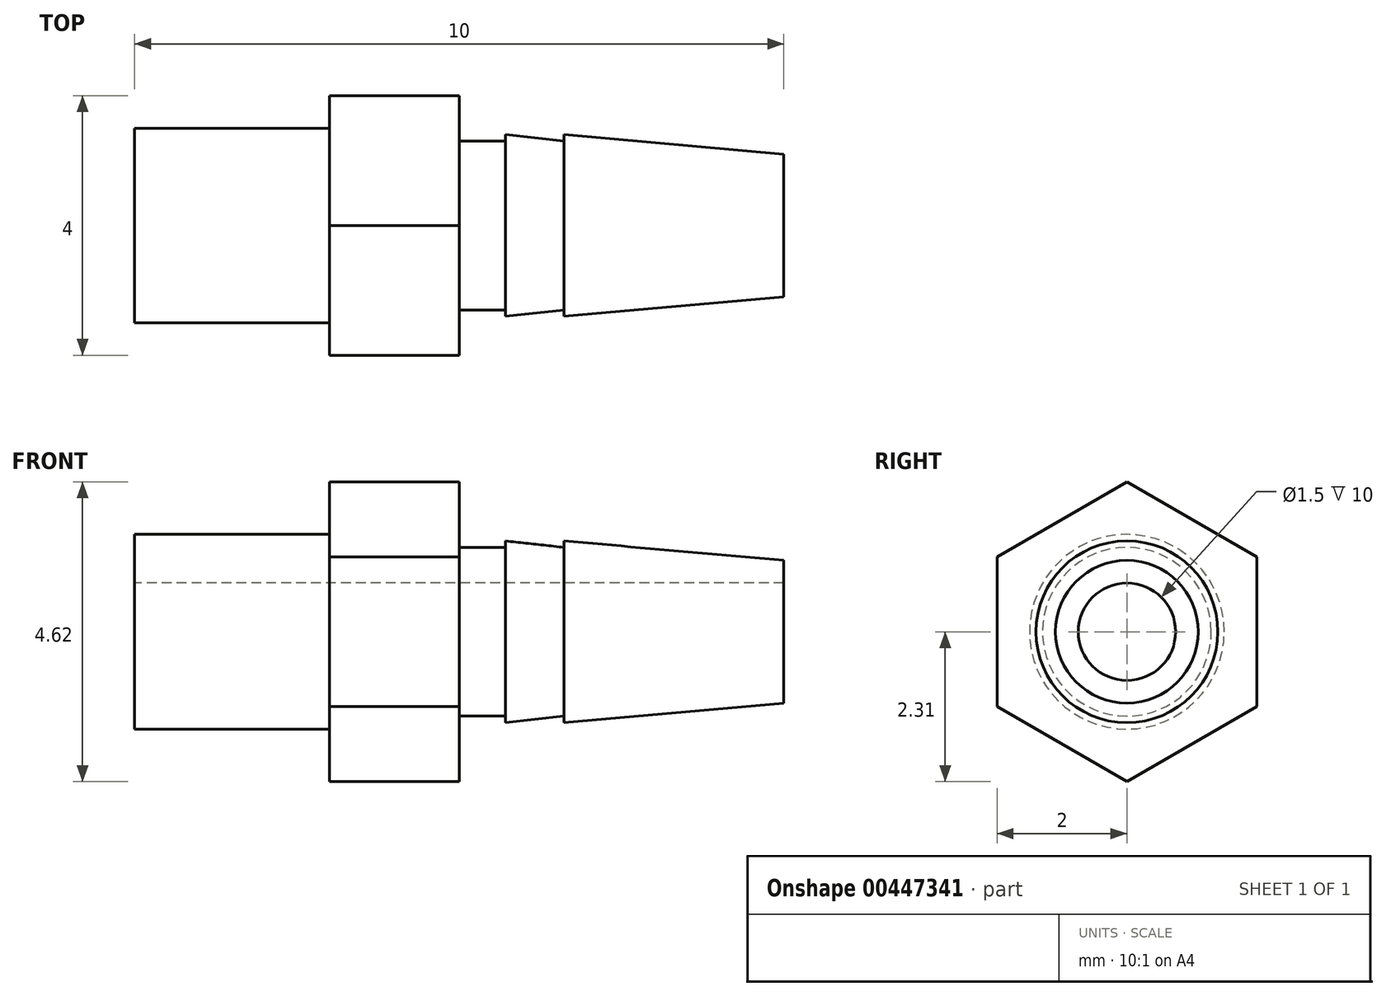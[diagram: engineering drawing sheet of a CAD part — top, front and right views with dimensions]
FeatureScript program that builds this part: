
annotation { "Feature Type Name" : "Feature", "Feature Type Description" : "" }
export const myFeature = defineFeature(function(context is Context, id is Id, definition is map)
    precondition{}
    {
        {
            var Q0;
            Q0=qCreatedBy(makeId("Top.planeOp"),FACE);
            var sketch = newSketch(context, id + "F0", { "sketchPlane" : qUnion([Q0])});
            skLineSegment(sketch, "E0", {"start": v(0, 0) * mm, "end": v(15.5, 0) * mm, "construction": true});
            skLineSegment(sketch, "E1", {"start": v(0, 0.75) * mm, "end": v(10, 0.75) * mm});
            skLineSegment(sketch, "E2", {"start": v(10, 0.75) * mm, "end": v(10, 1.1) * mm});
            skLineSegment(sketch, "E3", {"start": v(10, 1.1) * mm, "end": v(6.62, 1.4) * mm});
            skLineSegment(sketch, "E4", {"start": v(6.62, 1.4) * mm, "end": v(6.62, 1.3) * mm});
            skLineSegment(sketch, "E5", {"start": v(6.62, 1.3) * mm, "end": v(5.71, 1.4) * mm});
            skLineSegment(sketch, "E6", {"start": v(5.71, 1.4) * mm, "end": v(5.71, 1.3) * mm});
            skLineSegment(sketch, "E7", {"start": v(5.71, 1.3) * mm, "end": v(5, 1.3) * mm});
            skLineSegment(sketch, "E8", {"start": v(5, 1.3) * mm, "end": v(5, 2) * mm});
            skLineSegment(sketch, "E9", {"start": v(5, 2) * mm, "end": v(3, 2) * mm});
            skLineSegment(sketch, "E10", {"start": v(3, 2) * mm, "end": v(3, 1.5) * mm});
            skLineSegment(sketch, "E11", {"start": v(3, 1.5) * mm, "end": v(0, 1.5) * mm});
            skLineSegment(sketch, "E12", {"start": v(0, 1.5) * mm, "end": v(0, 0.75) * mm});
            skSolve(sketch);
        }
        {
            var Q0;
            Q0=makeQuery(id+"F0.imprint","IMPRINT",FACE,{"disambiguationData":[TD([[makeQuery(id+"F0.imprint","IMPRINT",EDGE,{"derivedFrom":sQuery(id+"F0.wireOp",EDGE,"E1")}),1.0]])]});
            var Q1;
            Q1=sQuery(id+"F0.wireOp",EDGE,"E0");
            revolve(context, id + "F1", {"entities" : qUnion([Q0]), "axis" : qUnion([Q1]), "revolveType" : RevolveType.FULL});
        }
        {
            var Q0;
            Q0=makeQuery(id+"F1.opRevolve","SWEPT_FACE",FACE,{"disambiguationData":[OSD([sQuery(id+"F0.wireOp",EDGE,"E8")])]});
            var sketch = newSketch(context, id + "F2", { "sketchPlane" : qUnion([Q0])});
            skLineSegment(sketch, "E13", {"start": v(0, 0) * mm, "end": v(2, 0) * mm, "construction": true});
            skCircle(sketch, "E14.cCircle", {"center": v(0, 0) * mm, "radius": 2 * mm, "construction": true});
            skLineSegment(sketch, "E14.0", {"start": v(2, 1.15) * mm, "end": v(2, -1.15) * mm});
            skLineSegment(sketch, "E14.1", {"start": v(2, -1.15) * mm, "end": v(0, -2.3) * mm});
            skLineSegment(sketch, "E14.2", {"start": v(0, -2.3) * mm, "end": v(-2, -1.15) * mm});
            skLineSegment(sketch, "E14.3", {"start": v(-2, -1.15) * mm, "end": v(-2, 1.15) * mm});
            skLineSegment(sketch, "E14.4", {"start": v(-2, 1.15) * mm, "end": v(0, 2.3) * mm});
            skLineSegment(sketch, "E14.5", {"start": v(0, 2.3) * mm, "end": v(2, 1.15) * mm});
            skPoint(sketch, "E14.0.midPoint", {"position": v(2, 0) * mm});
            skSolve(sketch);
        }
        {
            var Q0;
            {var subQ0=sQuery(id+"F2.wireOp",EDGE,"E14.3");var subQ1=sQuery(id+"F2.wireOp",EDGE,"E14.2");var subQ2=makeQuery(id+"F2.imprint","INTERSECT",VERTEX,{"derivedFrom":[subQ1,subQ0]});Q0=makeQuery(id+"F2.imprint","IMPRINT",FACE,{"disambiguationData":[TD([[makeQuery(id+"F2.imprint","IMPRINT",EDGE,{"disambiguationData":[TD([[subQ2,1.0]])],"derivedFrom":subQ1}),-1.0]])]});}
            var Q1;
            {var subQ0=sQuery(id+"F2.wireOp",EDGE,"E14.2");var subQ1=sQuery(id+"F2.wireOp",EDGE,"E14.1");var subQ2=makeQuery(id+"F2.imprint","INTERSECT",VERTEX,{"derivedFrom":[subQ1,subQ0]});Q1=makeQuery(id+"F2.imprint","IMPRINT",FACE,{"disambiguationData":[TD([[makeQuery(id+"F2.imprint","IMPRINT",EDGE,{"disambiguationData":[TD([[subQ2,1.0]])],"derivedFrom":subQ1}),-1.0]])]});}
            var Q2;
            {var subQ0=sQuery(id+"F2.wireOp",EDGE,"E14.4");var subQ1=sQuery(id+"F2.wireOp",EDGE,"E14.3");var subQ2=makeQuery(id+"F2.imprint","INTERSECT",VERTEX,{"derivedFrom":[subQ1,subQ0]});Q2=makeQuery(id+"F2.imprint","IMPRINT",FACE,{"disambiguationData":[TD([[makeQuery(id+"F2.imprint","IMPRINT",EDGE,{"disambiguationData":[TD([[subQ2,1.0]])],"derivedFrom":subQ1}),-1.0]])]});}
            var Q3;
            {var subQ0=sQuery(id+"F2.wireOp",EDGE,"E14.5");var subQ1=sQuery(id+"F2.wireOp",EDGE,"E14.4");var subQ2=makeQuery(id+"F2.imprint","INTERSECT",VERTEX,{"derivedFrom":[subQ1,subQ0]});Q3=makeQuery(id+"F2.imprint","IMPRINT",FACE,{"disambiguationData":[TD([[makeQuery(id+"F2.imprint","IMPRINT",EDGE,{"disambiguationData":[TD([[subQ2,1.0]])],"derivedFrom":subQ1}),-1.0]])]});}
            var Q4;
            {var subQ0=sQuery(id+"F2.wireOp",EDGE,"E14.5");var subQ1=sQuery(id+"F2.wireOp",EDGE,"E14.0");var subQ2=makeQuery(id+"F2.imprint","INTERSECT",VERTEX,{"derivedFrom":[subQ1,subQ0]});Q4=makeQuery(id+"F2.imprint","IMPRINT",FACE,{"disambiguationData":[TD([[makeQuery(id+"F2.imprint","IMPRINT",EDGE,{"disambiguationData":[TD([[subQ2,-1.0]])],"derivedFrom":subQ1}),-1.0]])]});}
            var Q5;
            {var subQ0=sQuery(id+"F2.wireOp",EDGE,"E14.1");var subQ1=sQuery(id+"F2.wireOp",EDGE,"E14.0");var subQ2=makeQuery(id+"F2.imprint","INTERSECT",VERTEX,{"derivedFrom":[subQ1,subQ0]});Q5=makeQuery(id+"F2.imprint","IMPRINT",FACE,{"disambiguationData":[TD([[makeQuery(id+"F2.imprint","IMPRINT",EDGE,{"disambiguationData":[TD([[subQ2,1.0]])],"derivedFrom":subQ1}),-1.0]])]});}
            var Q6;
            {var subQ0=sQuery(id+"F0.wireOp",EDGE,"E8");Q6=makeQuery(id+"F2.imprint","IMPRINT",FACE,{"disambiguationData":[TD([[makeQuery(id+"F2.imprint","IMPRINT",EDGE,{"derivedFrom":makeQuery(id+"F1.opRevolve","SWEPT_EDGE",EDGE,{"disambiguationData":[OSD([sQuery(id+"F0.wireOp",EDGE,"E7"),subQ0])]})}),1.0]])]});}
            extrude(context, id + "F3", {"entities" : qUnion([Q0, Q1, Q2, Q3, Q4, Q5, Q6]), "operationType" : NewBodyOperationType.ADD, "oppositeDirection" : true, "depth" : 2 * mm});
        }
    });
